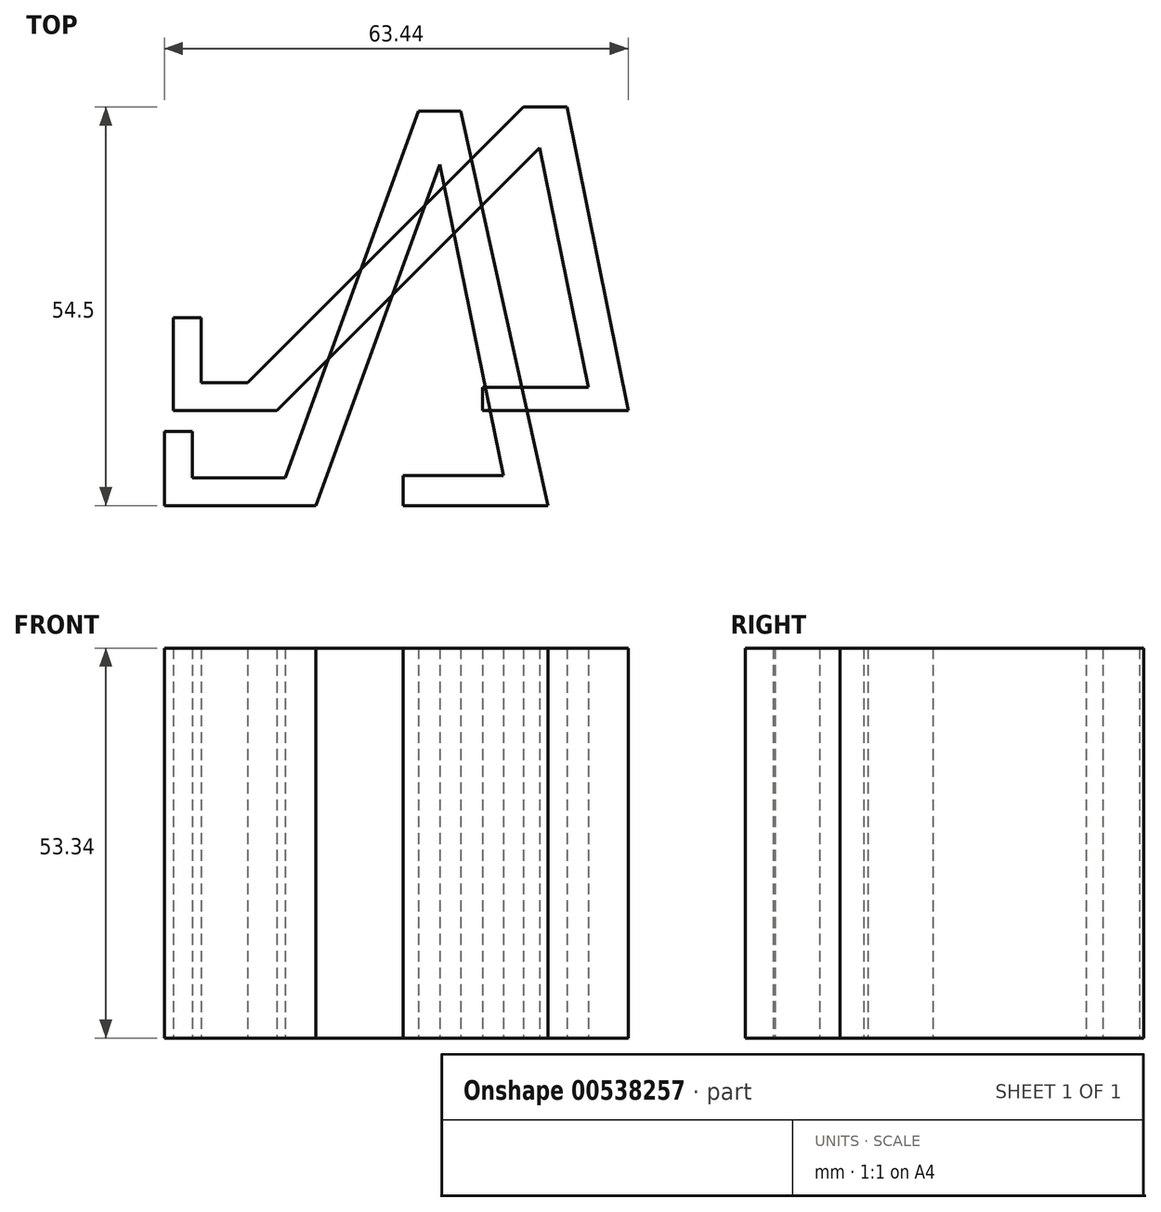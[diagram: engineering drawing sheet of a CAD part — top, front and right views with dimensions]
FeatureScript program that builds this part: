
annotation { "Feature Type Name" : "Feature", "Feature Type Description" : "" }
export const myFeature = defineFeature(function(context is Context, id is Id, definition is map)
    precondition{}
    {
        {
            var Q0;
            Q0=qCreatedBy(makeId("Top.planeOp"),FACE);
            var sketch = newSketch(context, id + "F0", { "sketchPlane" : qUnion([Q0])});
            skLineSegment(sketch, "E0", {"start": v(-25.88, 0) * mm, "end": v(42.34, 0) * mm, "construction": true});
            skLineSegment(sketch, "E1", {"start": v(0, 0) * mm, "end": v(-10.16, 0) * mm});
            skLineSegment(sketch, "E2", {"start": v(-10.16, 0) * mm, "end": v(-10.16, 10.16) * mm});
            skLineSegment(sketch, "E3", {"start": v(-10.16, 10.16) * mm, "end": v(-6.35, 10.16) * mm});
            skLineSegment(sketch, "E4", {"start": v(-6.35, 10.16) * mm, "end": v(-6.35, 3.81) * mm});
            skLineSegment(sketch, "E5", {"start": v(-6.35, 3.81) * mm, "end": v(0, 3.81) * mm});
            skLineSegment(sketch, "E6", {"start": v(0, 3.81) * mm, "end": v(6.35, 3.81) * mm});
            skLineSegment(sketch, "E7", {"start": v(6.35, 3.8) * mm, "end": v(24.6, 53.93) * mm});
            skLineSegment(sketch, "E8", {"start": v(24.6, 53.93) * mm, "end": v(30.4, 53.93) * mm});
            skLineSegment(sketch, "E9", {"start": v(30.4, 53.93) * mm, "end": v(42.34, 0) * mm});
            skLineSegment(sketch, "E10", {"start": v(-10.16, 0) * mm, "end": v(10.55, 0) * mm});
            skLineSegment(sketch, "E11", {"start": v(22.5, 0) * mm, "end": v(22.5, 4.07) * mm});
            skLineSegment(sketch, "E12", {"start": v(22.5, 4.07) * mm, "end": v(36.23, 4.07) * mm});
            skLineSegment(sketch, "E13", {"start": v(36.23, 4.07) * mm, "end": v(27.53, 46.66) * mm});
            skLineSegment(sketch, "E14", {"start": v(27.53, 46.66) * mm, "end": v(10.55, 0) * mm});
            skLineSegment(sketch, "E15.trimOffspring", {"start": v(22.5, 0) * mm, "end": v(42.34, 0) * mm});
            skSolve(sketch);
        }
        {
            var Q0;
            {var subQ1=sQuery(id+"F0.wireOp",EDGE,"E2");Q0=makeQuery(id+"F0.imprint","IMPRINT",FACE,{"disambiguationData":[TD([[makeQuery(id+"F0.imprint","IMPRINT",EDGE,{"derivedFrom":subQ1}),-1.0]])]});}
            extrude(context, id + "F1", {"entities" : qUnion([Q0]), "depth" : 53.34 * mm, "offsetDistance" : 25.4 * mm});
        }
        {
            var Q0;
            Q0=qCreatedBy(makeId("Top.planeOp"),FACE);
            var sketch = newSketch(context, id + "F2", { "sketchPlane" : qUnion([Q0])});
            skLineSegment(sketch, "E16", {"start": v(-29.52, 12.97) * mm, "end": v(53.28, 12.97) * mm, "construction": true});
            skLineSegment(sketch, "E17", {"start": v(-3.64, 12.97) * mm, "end": v(-8.94, 12.97) * mm});
            skLineSegment(sketch, "E18", {"start": v(-8.94, 12.97) * mm, "end": v(-8.94, 25.67) * mm});
            skLineSegment(sketch, "E19", {"start": v(-8.94, 25.67) * mm, "end": v(-5.13, 25.67) * mm});
            skLineSegment(sketch, "E20", {"start": v(-5.13, 25.67) * mm, "end": v(-5.13, 16.78) * mm});
            skLineSegment(sketch, "E21", {"start": v(-5.13, 16.78) * mm, "end": v(-1.95, 16.78) * mm});
            skLineSegment(sketch, "E22", {"start": v(-1.95, 16.78) * mm, "end": v(1.22, 16.78) * mm});
            skLineSegment(sketch, "E23", {"start": v(1.22, 16.78) * mm, "end": v(38.94, 54.5) * mm});
            skLineSegment(sketch, "E24", {"start": v(38.94, 54.5) * mm, "end": v(44.9, 54.5) * mm});
            skLineSegment(sketch, "E25", {"start": v(-8.94, 12.97) * mm, "end": v(5.24, 12.97) * mm});
            skLineSegment(sketch, "E26", {"start": v(33.35, 12.97) * mm, "end": v(33.35, 16.2) * mm});
            skLineSegment(sketch, "E27", {"start": v(33.35, 16.2) * mm, "end": v(47.86, 16.2) * mm});
            skLineSegment(sketch, "E28", {"start": v(47.86, 16.2) * mm, "end": v(41.18, 48.91) * mm});
            skLineSegment(sketch, "E29", {"start": v(41.18, 48.91) * mm, "end": v(5.24, 12.97) * mm});
            skLineSegment(sketch, "E30.trimOffspring", {"start": v(33.35, 12.97) * mm, "end": v(53.28, 12.97) * mm});
            skLineSegment(sketch, "E31", {"start": v(44.9, 54.5) * mm, "end": v(53.28, 12.97) * mm});
            skSolve(sketch);
        }
        {
            var Q0;
            {var subQ1=sQuery(id+"F2.wireOp",EDGE,"E18");Q0=makeQuery(id+"F2.imprint","IMPRINT",FACE,{"disambiguationData":[TD([[makeQuery(id+"F2.imprint","IMPRINT",EDGE,{"derivedFrom":subQ1}),-1.0]])]});}
            extrude(context, id + "F3", {"entities" : qUnion([Q0]), "depth" : 53.34 * mm, "offsetDistance" : 25.4 * mm});
        }
    });
